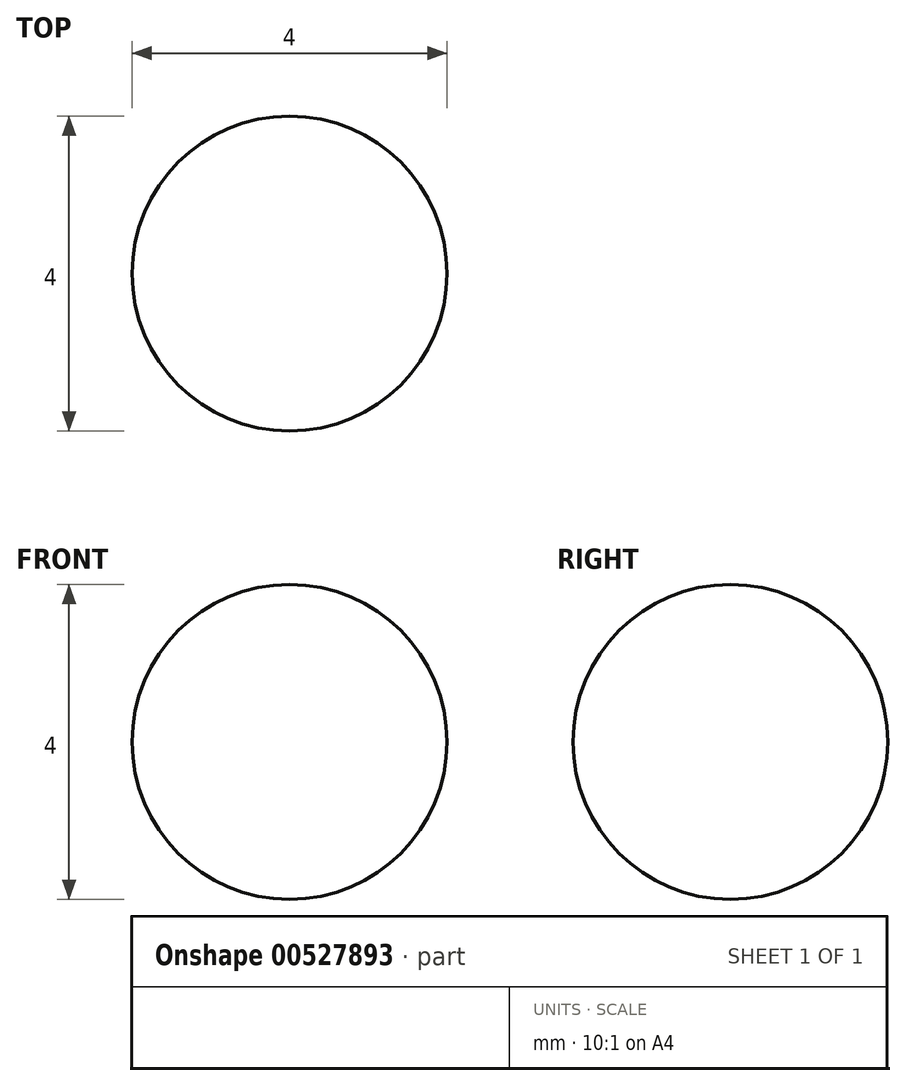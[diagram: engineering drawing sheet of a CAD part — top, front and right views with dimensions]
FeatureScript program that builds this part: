
annotation { "Feature Type Name" : "Feature", "Feature Type Description" : "" }
export const myFeature = defineFeature(function(context is Context, id is Id, definition is map)
    precondition{}
    {
        {
            var Q0;
            Q0=qCreatedBy(makeId("Front.planeOp"),FACE);
            var sketch = newSketch(context, id + "F0", { "sketchPlane" : qUnion([Q0])});
            skLineSegment(sketch, "E0", {"start": v(0, 0) * mm, "end": v(0, 4) * mm});
            skArc(sketch, "E1", {"start": v(0, 0) * mm, "mid": v(2, 2) * mm, "end": v(0, 4) * mm});
            skSolve(sketch);
        }
        {
            var Q0;
            Q0=qSketchRegion(id+"F0",true);
            var Q1;
            Q1=sQuery(id+"F0.wireOp",EDGE,"E0");
            revolve(context, id + "F1", {"entities" : qUnion([Q0]), "axis" : qUnion([Q1]), "revolveType" : RevolveType.FULL});
        }
    });
